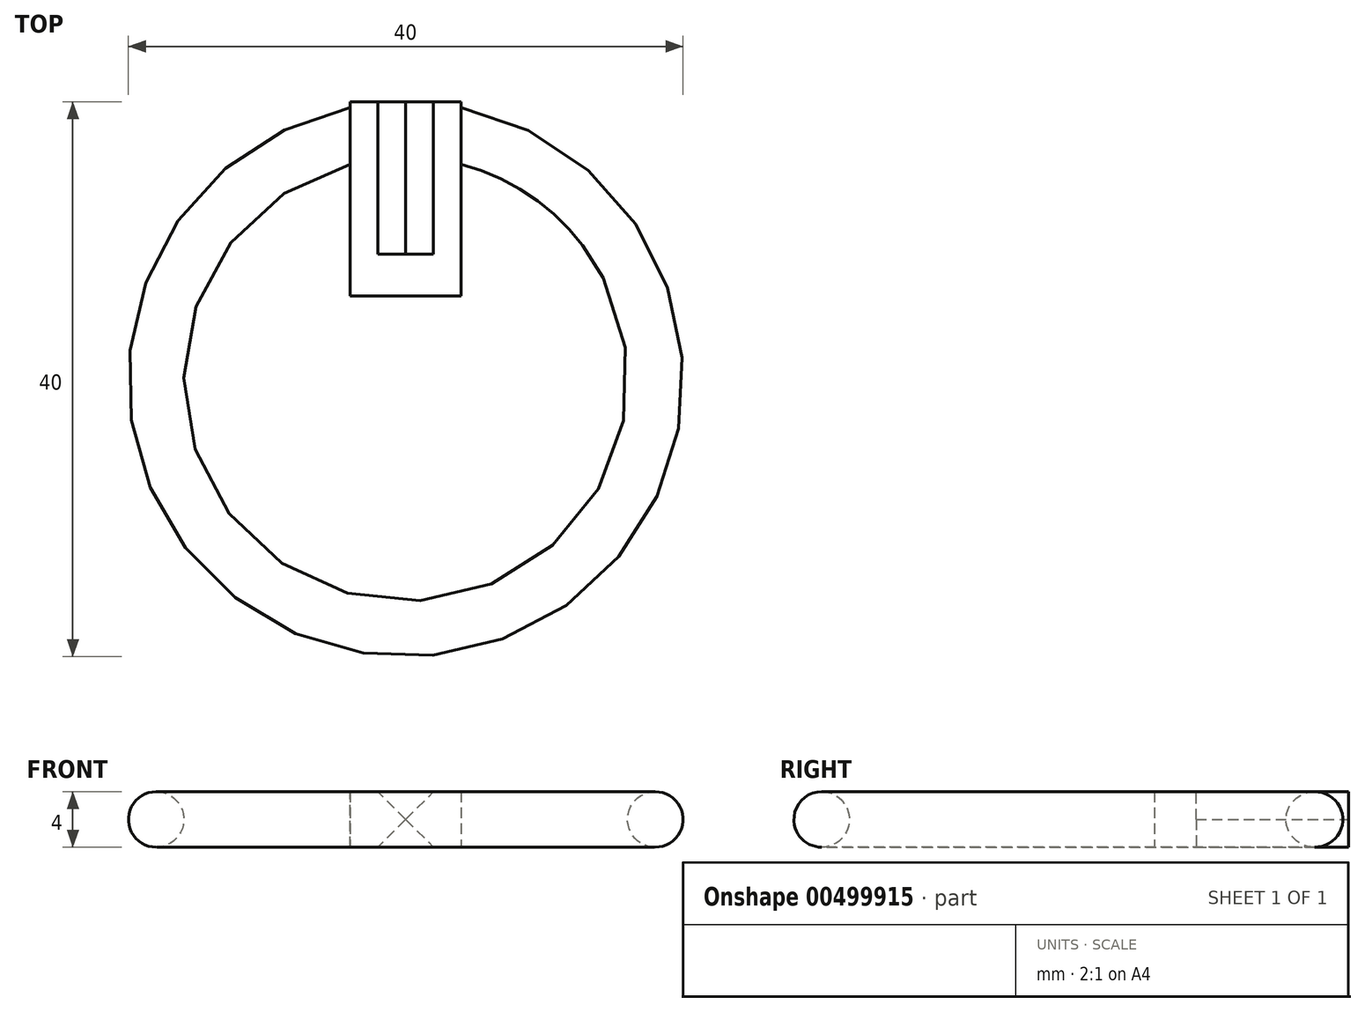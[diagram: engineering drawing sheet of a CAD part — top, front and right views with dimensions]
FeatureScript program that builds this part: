
annotation { "Feature Type Name" : "Feature", "Feature Type Description" : "" }
export const myFeature = defineFeature(function(context is Context, id is Id, definition is map)
    precondition{}
    {
        {
            var Q0;
            Q0=qCreatedBy(makeId("Top.planeOp"),FACE);
            var sketch = newSketch(context, id + "F0", { "sketchPlane" : qUnion([Q0])});
            skCircle(sketch, "E0", {"center": v(0, 0) * mm, "radius": 20 * mm});
            skCircle(sketch, "E1.0", {"center": v(0, 0) * mm, "radius": 16 * mm});
            skLineSegment(sketch, "E2", {"start": v(0, 6) * mm, "end": v(-4, 6) * mm});
            skLineSegment(sketch, "E3", {"start": v(0, 6) * mm, "end": v(4, 6) * mm});
            skLineSegment(sketch, "E4", {"start": v(-4, 6) * mm, "end": v(-4, 15.5) * mm});
            skLineSegment(sketch, "E5", {"start": v(4, 6) * mm, "end": v(4, 15.5) * mm});
            skPoint(sketch, "E6.start.orphan", {"position": v(0, 20) * mm});
            skLineSegment(sketch, "E7", {"start": v(4, 15.5) * mm, "end": v(4, 19.6) * mm});
            skLineSegment(sketch, "E8", {"start": v(-4, 15.5) * mm, "end": v(-4, 19.6) * mm});
            skLineSegment(sketch, "E9", {"start": v(4, 19.6) * mm, "end": v(-4, 19.6) * mm});
            skSolve(sketch);
        }
        {
            var Q0;
            Q0=qCreatedBy(makeId("Front.planeOp"),FACE);
            var sketch = newSketch(context, id + "F1", { "sketchPlane" : qUnion([Q0])});
            skCircle(sketch, "E10", {"center": v(18, 0) * mm, "radius": 2 * mm});
            skPoint(sketch, "E11.start.orphan", {"position": v(20, 0) * mm});
            skSolve(sketch);
        }
        {
            var Q0;
            Q0=makeQuery(id+"F1.imprint","IMPRINT",FACE,{"disambiguationData":[TD([[makeQuery(id+"F1.imprint","IMPRINT",EDGE,{"derivedFrom":sQuery(id+"F1.wireOp",EDGE,"E10")}),1.0]])]});
            var Q1;
            Q1=sQuery(id+"F0.wireOp",EDGE,"E0");
            revolve(context, id + "F2", {"entities" : qUnion([Q0]), "axis" : qUnion([Q1]), "revolveType" : RevolveType.FULL});
        }
        {
            var Q0;
            Q0=makeQuery(id+"F0.imprint","IMPRINT",FACE,{"disambiguationData":[TD([[makeQuery(id+"F0.imprint","IMPRINT",EDGE,{"derivedFrom":sQuery(id+"F0.wireOp",EDGE,"E2")}),-1.0]])]});
            var sketch = newSketch(context, id + "F3", { "sketchPlane" : qUnion([Q0])});
            skLineSegment(sketch, "E12", {"start": v(0, 20) * mm, "end": v(-4, 20) * mm});
            skLineSegment(sketch, "E13", {"start": v(0, 20) * mm, "end": v(4, 20) * mm});
            skLineSegment(sketch, "E14", {"start": v(4, 20) * mm, "end": v(4, 6) * mm});
            skLineSegment(sketch, "E15", {"start": v(4, 6) * mm, "end": v(-4, 6) * mm});
            skLineSegment(sketch, "E16", {"start": v(-4, 6) * mm, "end": v(-4, 20) * mm});
            skLineSegment(sketch, "E17", {"start": v(0, 6) * mm, "end": v(0, 8.15) * mm});
            skPoint(sketch, "E17.endSnap0", {"position": v(0, 6) * mm});
            skPoint(sketch, "E18.visualSharp", {"position": v(-3.79, 2.1) * mm});
            skPoint(sketch, "E19.visualSharp", {"position": v(-2, -4.65) * mm});
            skPoint(sketch, "E20.start.orphan", {"position": v(2, -4.65) * mm});
            skPoint(sketch, "E21.end.orphan", {"position": v(3.79, 2.1) * mm});
            skPoint(sketch, "E22.end.orphan", {"position": v(7.45, -1.3) * mm});
            skPoint(sketch, "E23.MirrorCS.end.orphan", {"position": v(9.5, 0.9) * mm});
            skPoint(sketch, "E23.MirrorCS.start.orphan", {"position": v(4, 6) * mm});
            skPoint(sketch, "E24.visualSharp", {"position": v(-9.5, 0.9) * mm});
            skPoint(sketch, "E25.visualSharp", {"position": v(-7.45, -1.3) * mm});
            skPoint(sketch, "E26.start.orphan", {"position": v(0, -4.65) * mm});
            skSolve(sketch);
        }
        {
            var Q0;
            Q0 = qSketchRegion(id + "F3", true);
            extrude(context, id + "F4", {"entities" : qUnion([Q0]), "operationType" : NewBodyOperationType.ADD, "depth" : 2 * mm, "hasSecondDirection" : true, "secondDirectionOppositeDirection" : true, "secondDirectionDepth" : 2 * mm});
        }
        {
            var Q0;
            Q0=makeQuery(id+"F4.opExtrude","SWEPT_FACE",FACE,{"disambiguationData":[OSD([sQuery(id+"F3.wireOp",EDGE,"E12"),sQuery(id+"F3.wireOp",EDGE,"E13")])]});
            var sketch = newSketch(context, id + "F5", { "sketchPlane" : qUnion([Q0])});
            skLineSegment(sketch, "E27", {"start": v(-2, -2) * mm, "end": v(2, -2) * mm});
            skLineSegment(sketch, "E28", {"start": v(2, 2) * mm, "end": v(-2, 2) * mm});
            skPoint(sketch, "E29.orphan", {"position": v(4, -2) * mm});
            skPoint(sketch, "E30.orphan", {"position": v(-4, 2) * mm});
            skLineSegment(sketch, "E31", {"start": v(0, 0) * mm, "end": v(-2, 2) * mm});
            skLineSegment(sketch, "E32", {"start": v(0, 0) * mm, "end": v(-2, -2) * mm});
            skLineSegment(sketch, "E33.MirrorCS", {"start": v(0, 0) * mm, "end": v(2, 2) * mm});
            skLineSegment(sketch, "E34.MirrorCS", {"start": v(0, 0) * mm, "end": v(2, -2) * mm});
            skPoint(sketch, "E35.start.orphan", {"position": v(0, 0) * mm});
            skPoint(sketch, "E36.orphan", {"position": v(0, 2) * mm});
            skPoint(sketch, "E37.end.orphan", {"position": v(0, -2) * mm});
            skPoint(sketch, "E38.orphan", {"position": v(-3, 2) * mm});
            skPoint(sketch, "E39.orphan", {"position": v(-3, -2) * mm});
            skPoint(sketch, "E40.orphan", {"position": v(3, -2) * mm});
            skPoint(sketch, "E41.orphan", {"position": v(3, 2) * mm});
            skSolve(sketch);
        }
        {
            var Q0;
            Q0 = qSketchRegion(id + "F5", true);
            extrude(context, id + "F6", {"entities" : qUnion([Q0]), "operationType" : NewBodyOperationType.REMOVE, "oppositeDirection" : true, "depth" : 11 * mm});
        }
    });
